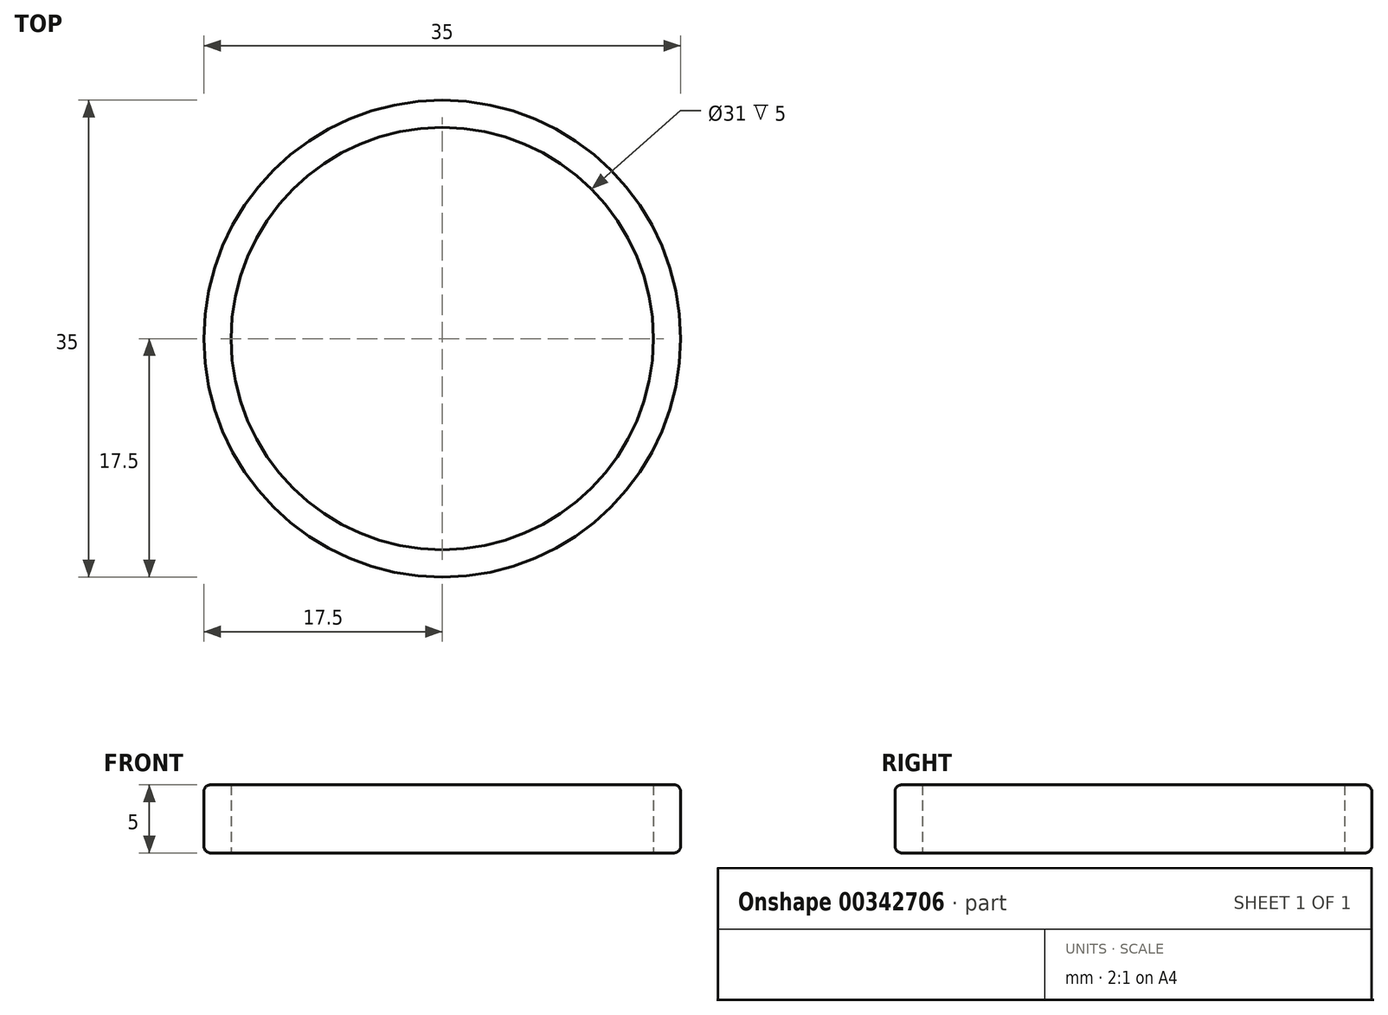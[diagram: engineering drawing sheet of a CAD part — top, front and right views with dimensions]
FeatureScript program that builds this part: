
annotation { "Feature Type Name" : "Feature", "Feature Type Description" : "" }
export const myFeature = defineFeature(function(context is Context, id is Id, definition is map)
    precondition{}
    {
        {
            var Q0;
            Q0=qCreatedBy(makeId("Top.planeOp"),FACE);
            var sketch = newSketch(context, id + "F0", { "sketchPlane" : qUnion([Q0])});
            skCircle(sketch, "E0", {"center": v(0, 0) * mm, "radius": 17.5 * mm});
            skCircle(sketch, "E1.0", {"center": v(0, 0) * mm, "radius": 15.5 * mm});
            skSolve(sketch);
        }
        {
            var Q0;
            Q0=makeQuery(id+"F0.imprint","IMPRINT",FACE,{"disambiguationData":[TD([[makeQuery(id+"F0.imprint","IMPRINT",EDGE,{"derivedFrom":sQuery(id+"F0.wireOp",EDGE,"E0")}),1.0]])]});
            extrude(context, id + "F1", {"entities" : qUnion([Q0]), "depth" : 5 * mm});
        }
        {
            var Q0;
            Q0=makeQuery(id+"F0.imprint","IMPRINT",FACE,{"disambiguationData":[TD([[makeQuery(id+"F0.imprint","IMPRINT",EDGE,{"derivedFrom":sQuery(id+"F0.wireOp",EDGE,"E1.0")}),1.0]])]});
            extrude(context, id + "F2", {"entities" : qUnion([Q0]), "depth" : 5 * mm});
        }
        {
            var Q0;
            Q0=makeQuery(id+"F1.opExtrude","CAP_EDGE",EDGE,{"disambiguationData":[OSD([sQuery(id+"F0.wireOp",EDGE,"E0")])],"isStart":false});
            var Q1;
            Q1=makeQuery(id+"F1.opExtrude","CAP_EDGE",EDGE,{"disambiguationData":[OSD([sQuery(id+"F0.wireOp",EDGE,"E0")])],"isStart":true});
            fillet(context, id + "F3", {"entities" : qUnion([Q0, Q1]), "radius" : 0.5 * mm, "tangentPropagation" : true, "allowEdgeOverflow" : false});
        }
    });
